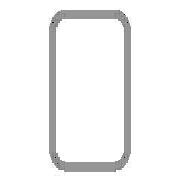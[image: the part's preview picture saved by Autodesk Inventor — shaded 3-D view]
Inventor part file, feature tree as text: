
AUTODESK INVENTOR PART (.ipt)
format: ipt  version: 2025 (Build 290162010, 162A)  size: 149,504 bytes
history: native  units: mm (DEFAULTED — no unit token found)
features: other x4, plane x3, split x2, sketch x1
ambient origin geometry x8: Origin, YZ Plane, XZ Plane, XY Plane, X Axis, Y Axis, Z Axis, Center Point
bodies: Solid1 (feature_tree), Body (feature_tree)
feature tree (10):
  parser-record x1  (decoder bookkeeping rows leaked as tree rows — omitted from the tree; the rows remain in map.json)
  other  "Driven Length"
  other  "Start Plane"
  other  "End Plane"
  plane  "Work Plane4"
  split  "Split1"
  plane  "Work Plane5"
  split  "Split2"
  sketch  "Sketch3"  dims[d3=615.253612mm d4=0.0mm d7=4.0mm d9=20.0mm d11=40.0mm d12=2.0mm d13=17.365243mm d14=632.618856mm d15=10.0mm d16=20.0mm d17=90.0deg d18=615.253612mm]
  plane  "Work Plane3"
